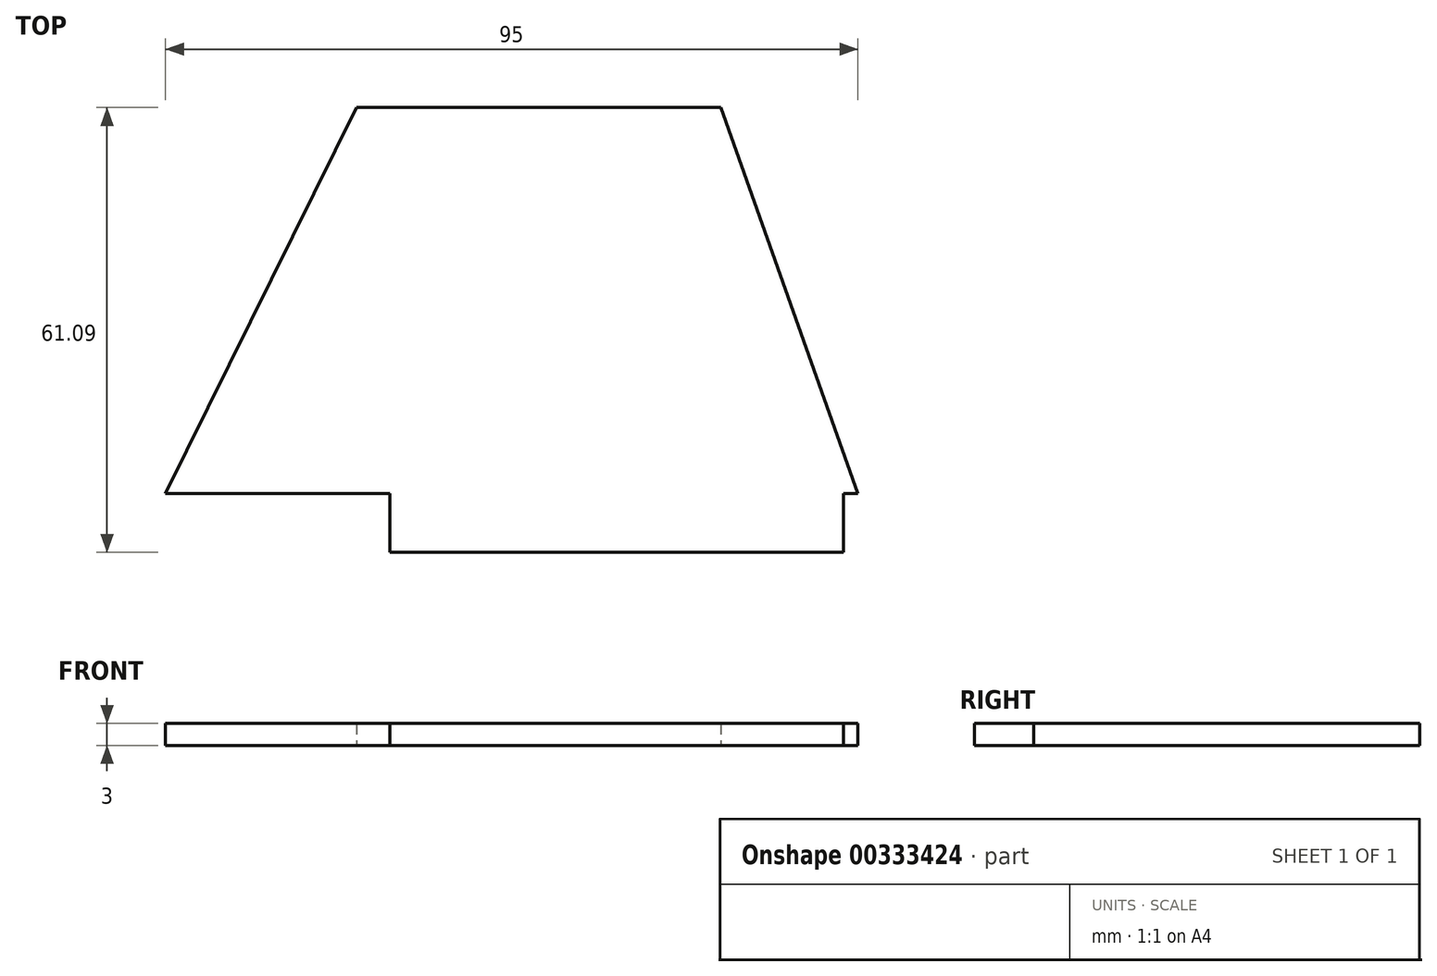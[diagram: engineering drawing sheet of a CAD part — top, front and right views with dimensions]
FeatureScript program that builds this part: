
annotation { "Feature Type Name" : "Feature", "Feature Type Description" : "" }
export const myFeature = defineFeature(function(context is Context, id is Id, definition is map)
    precondition{}
    {
        {
            var Q0;
            Q0=qCreatedBy(makeId("Top.planeOp"),FACE);
            var sketch = newSketch(context, id + "F0", { "sketchPlane" : qUnion([Q0])});
            skLineSegment(sketch, "E0", {"start": v(0, 0) * mm, "end": v(-26.2, -53) * mm});
            skLineSegment(sketch, "E1", {"start": v(-26.2, -53) * mm, "end": v(68.8, -53) * mm});
            skLineSegment(sketch, "E2", {"start": v(68.8, -53) * mm, "end": v(50, 0) * mm});
            skLineSegment(sketch, "E3", {"start": v(50, 0) * mm, "end": v(0, 0) * mm});
            skLineSegment(sketch, "E4", {"start": v(0, 0) * mm, "end": v(0, -53) * mm, "construction": true});
            skLineSegment(sketch, "E5", {"start": v(50, 0) * mm, "end": v(50, -53) * mm, "construction": true});
            skLineSegment(sketch, "E6.bottom", {"start": v(66.8, -53) * mm, "end": v(50, -53) * mm, "construction": true});
            skLineSegment(sketch, "E6.top", {"start": v(66.8, -61.09) * mm, "end": v(4.6, -61.09) * mm});
            skLineSegment(sketch, "E6.left", {"start": v(66.8, -53) * mm, "end": v(66.8, -61.09) * mm});
            skLineSegment(sketch, "E6.right", {"start": v(4.6, -53) * mm, "end": v(4.6, -61.09) * mm});
            skSolve(sketch);
        }
        {
            var Q0;
            Q0 = qSketchRegion(id + "F0", true);
            extrude(context, id + "F1", {"entities" : qUnion([Q0]), "depth" : 3 * mm});
        }
    });
